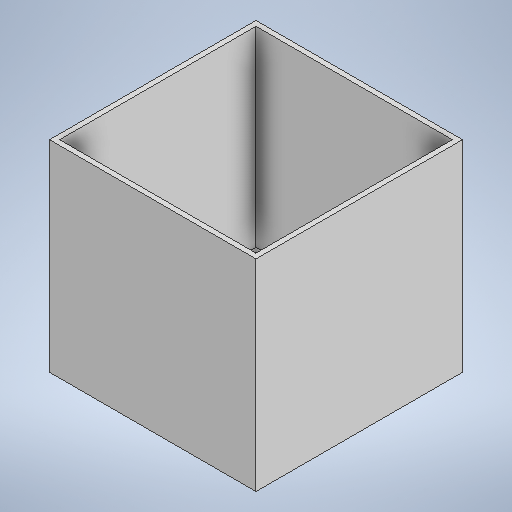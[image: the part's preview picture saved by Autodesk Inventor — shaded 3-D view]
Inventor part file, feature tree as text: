
AUTODESK INVENTOR PART (.ipt)
format: ipt  version: 2025.1 (Build 291241000, 241)  size: 187,392 bytes
history: native  units: mm
features: extrude x2, sketch x2, other x1
ambient origin geometry x8: Origin, YZ Plane, XZ Plane, XY Plane, X Axis, Y Axis, Z Axis, Center Point
bodies: Body1 (feature_tree)
feature tree (5):
  other  "Sólido1"
  extrude  "Extrusão1"  Depth=205.0mm
  extrude  "Extrusão2"  Depth=190.0mm
  sketch  "Esboço1"  dims[d0=205.0mm d1=205.0mm]
  sketch  "Esboço2"  dims[d2=102.5mm d3=102.5mm d4=200.0mm d5=0.0mm d6=5.0mm d7=5.0mm d8=5.0mm d9=5.0mm d10=190.0mm d11=0.0mm]
